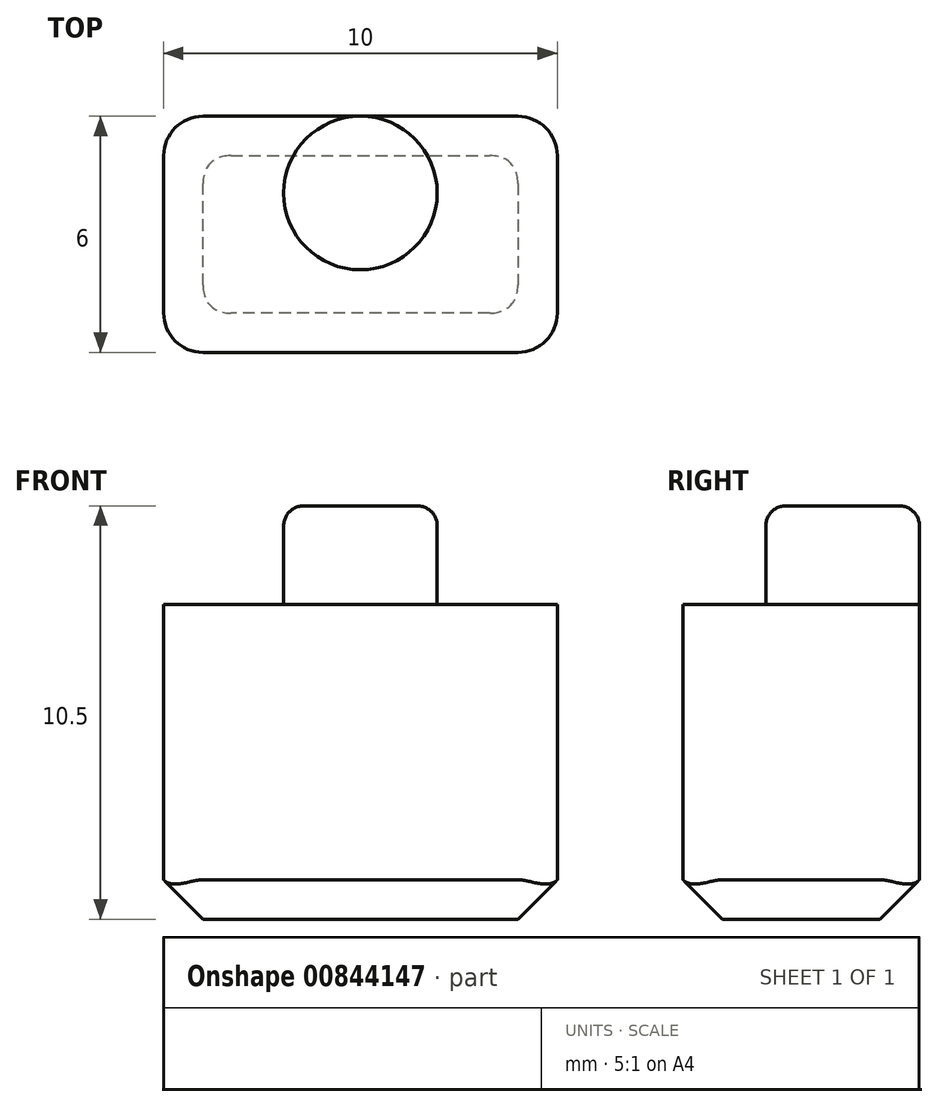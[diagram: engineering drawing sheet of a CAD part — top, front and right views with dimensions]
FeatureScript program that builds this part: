
annotation { "Feature Type Name" : "Feature", "Feature Type Description" : "" }
export const myFeature = defineFeature(function(context is Context, id is Id, definition is map)
    precondition{}
    {
        {
            var Q0;
            Q0=qCreatedBy(makeId("Top.planeOp"),FACE);
            var sketch = newSketch(context, id + "F0", { "sketchPlane" : qUnion([Q0])});
            skLineSegment(sketch, "E0.bottom", {"start": v(5, -3) * mm, "end": v(-5, -3) * mm});
            skLineSegment(sketch, "E0.top", {"start": v(5, 3) * mm, "end": v(-5, 3) * mm});
            skLineSegment(sketch, "E0.left", {"start": v(5, -3) * mm, "end": v(5, 3) * mm});
            skLineSegment(sketch, "E0.right", {"start": v(-5, -3) * mm, "end": v(-5, 3) * mm});
            skPoint(sketch, "E0.middle", {"position": v(0, 0) * mm});
            skCircle(sketch, "E1", {"center": v(0, 1.05) * mm, "radius": 1.95 * mm});
            skSolve(sketch);
        }
        {
            var Q0;
            Q0 = qSketchRegion(id + "F0", true);
            extrude(context, id + "F1", {"entities" : qUnion([Q0]), "oppositeDirection" : true, "depth" : 8 * mm, "offsetDistance" : 25 * mm});
        }
        {
            var Q0;
            Q0=makeQuery(id+"F0.imprint","IMPRINT",FACE,{"disambiguationData":[TD([[makeQuery(id+"F0.imprint","IMPRINT",EDGE,{"derivedFrom":sQuery(id+"F0.wireOp",EDGE,"E1")}),1.0]])]});
            extrude(context, id + "F2", {"entities" : qUnion([Q0]), "operationType" : NewBodyOperationType.ADD, "depth" : 2.5 * mm, "offsetDistance" : 25 * mm});
        }
        {
            var Q0;
            Q0=makeQuery(id+"F2.opExtrude","CAP_EDGE",EDGE,{"disambiguationData":[OSD([sQuery(id+"F0.wireOp",EDGE,"E1")])],"isStart":false});
            fillet(context, id + "F3", {"entities" : qUnion([Q0]), "radius" : 0.5 * mm, "tangentPropagation" : true, "allowEdgeOverflow" : false});
        }
        {
            var Q0;
            Q0=makeQuery(id+"F1.opExtrude","CAP_EDGE",EDGE,{"disambiguationData":[OSD([sQuery(id+"F0.wireOp",EDGE,"E0.right")])],"isStart":false});
            var Q1;
            Q1=makeQuery(id+"F1.opExtrude","CAP_EDGE",EDGE,{"disambiguationData":[OSD([sQuery(id+"F0.wireOp",EDGE,"E0.bottom")])],"isStart":false});
            var Q2;
            Q2=makeQuery(id+"F1.opExtrude","CAP_EDGE",EDGE,{"disambiguationData":[OSD([sQuery(id+"F0.wireOp",EDGE,"E0.top")])],"isStart":false});
            var Q3;
            Q3=makeQuery(id+"F1.opExtrude","CAP_EDGE",EDGE,{"disambiguationData":[OSD([sQuery(id+"F0.wireOp",EDGE,"E0.left")])],"isStart":false});
            chamfer(context, id + "F4", {"entities" : qUnion([Q0, Q1, Q2, Q3]), "width" : 1 * mm, "tangentPropagation" : true});
        }
        {
            var Q0;
            Q0=makeQuery(id+"F1.opExtrude","SWEPT_EDGE",EDGE,{"disambiguationData":[OSD([sQuery(id+"F0.wireOp",EDGE,"E0.top"),sQuery(id+"F0.wireOp",EDGE,"E0.left")])]});
            var Q1;
            Q1=makeQuery(id+"F1.opExtrude","SWEPT_EDGE",EDGE,{"disambiguationData":[OSD([sQuery(id+"F0.wireOp",EDGE,"E0.top"),sQuery(id+"F0.wireOp",EDGE,"E0.right")])]});
            var Q2;
            Q2=makeQuery(id+"F4.opChamfer","BLEND_EDGE",EDGE,{"blendedFrom":[makeQuery(id+"F1.opExtrude","CAP_EDGE",EDGE,{"disambiguationData":[OSD([sQuery(id+"F0.wireOp",EDGE,"E0.top")])],"isStart":false}),makeQuery(id+"F1.opExtrude","CAP_EDGE",EDGE,{"disambiguationData":[OSD([sQuery(id+"F0.wireOp",EDGE,"E0.right")])],"isStart":false})],"blendedInto":[]});
            var Q3;
            Q3=makeQuery(id+"F4.opChamfer","BLEND_EDGE",EDGE,{"blendedFrom":[makeQuery(id+"F1.opExtrude","CAP_EDGE",EDGE,{"disambiguationData":[OSD([sQuery(id+"F0.wireOp",EDGE,"E0.top")])],"isStart":false}),makeQuery(id+"F1.opExtrude","CAP_EDGE",EDGE,{"disambiguationData":[OSD([sQuery(id+"F0.wireOp",EDGE,"E0.left")])],"isStart":false})],"blendedInto":[]});
            var Q4;
            Q4=makeQuery(id+"F4.opChamfer","BLEND_EDGE",EDGE,{"blendedFrom":[makeQuery(id+"F1.opExtrude","CAP_EDGE",EDGE,{"disambiguationData":[OSD([sQuery(id+"F0.wireOp",EDGE,"E0.bottom")])],"isStart":false}),makeQuery(id+"F1.opExtrude","CAP_EDGE",EDGE,{"disambiguationData":[OSD([sQuery(id+"F0.wireOp",EDGE,"E0.left")])],"isStart":false})],"blendedInto":[]});
            var Q5;
            Q5=makeQuery(id+"F4.opChamfer","BLEND_EDGE",EDGE,{"blendedFrom":[makeQuery(id+"F1.opExtrude","CAP_EDGE",EDGE,{"disambiguationData":[OSD([sQuery(id+"F0.wireOp",EDGE,"E0.bottom")])],"isStart":false}),makeQuery(id+"F1.opExtrude","CAP_EDGE",EDGE,{"disambiguationData":[OSD([sQuery(id+"F0.wireOp",EDGE,"E0.right")])],"isStart":false})],"blendedInto":[]});
            var Q6;
            Q6=makeQuery(id+"F1.opExtrude","SWEPT_EDGE",EDGE,{"disambiguationData":[OSD([sQuery(id+"F0.wireOp",EDGE,"E0.bottom"),sQuery(id+"F0.wireOp",EDGE,"E0.left")])]});
            var Q7;
            Q7=makeQuery(id+"F1.opExtrude","SWEPT_EDGE",EDGE,{"disambiguationData":[OSD([sQuery(id+"F0.wireOp",EDGE,"E0.bottom"),sQuery(id+"F0.wireOp",EDGE,"E0.right")])]});
            fillet(context, id + "F5", {"entities" : qUnion([Q0, Q1, Q2, Q3, Q4, Q5, Q6, Q7]), "radius" : 1 * mm, "tangentPropagation" : true, "allowEdgeOverflow" : false});
        }
    });
